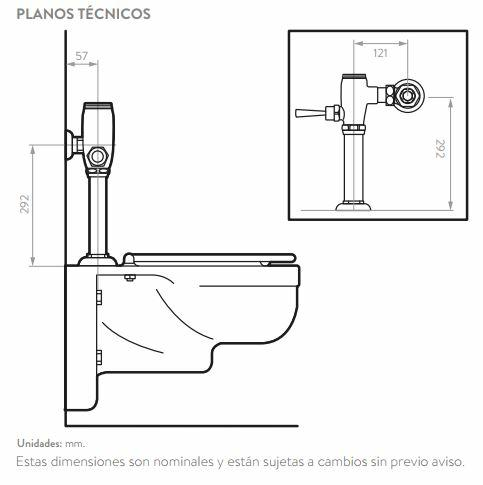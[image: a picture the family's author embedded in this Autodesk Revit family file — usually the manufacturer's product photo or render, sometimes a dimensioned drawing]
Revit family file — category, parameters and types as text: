
# Revit family: 707210001_Fluxómetro Palanca Sanitario
name_source: partatom
category: Plumbing Fixtures
units: mm (PartAtom-declared; Revit-internal decimal feet)

## family parameters
Always vertical = Yes
Cut with Voids When Loaded = No
Host = Wall
OmniClass Number = 23.45.55.11
OmniClass Title = Sanitary Components
Part Type = Normal
Room Calculation Point = No
Round Connector Dimension = Use Diameter
Shared = No

## types (1)
- Type 1
    Alto = 342 mm  [stored 1.12205 ft]
    Ancho = 289 mm
    Capacidad de flujo = 4,7 L/min a 50 PSI
    Creado por = IDD
    Dimensiones generales producto (H * W * D) = 329 x 85 x 291 mm.
13 x 3 x 11 pulg.
    Fabricante = Corona
    Fecha de creación = 31/07/2020
    Garantía = 3 años
    Material = Corona_Acero
    Peso Bruto aprox = 2,370 gr. 5,2250 lb
    Peso Neto aprox = 2,130 gr. 4,6959 lb
    Presion maxima = 80 psi
    Presion minima = 35 psi
    Profundidad = 97 mm
    Referencia = 707210001
    URL = https://corona.co

note: [stored X ft] marks values corroborated as IEEE doubles in the binary element streams (Revit-internal decimal feet)

## geometry (parser evidence)
native form markers: Sweep x4
no freeform markers — native parametric forms only
